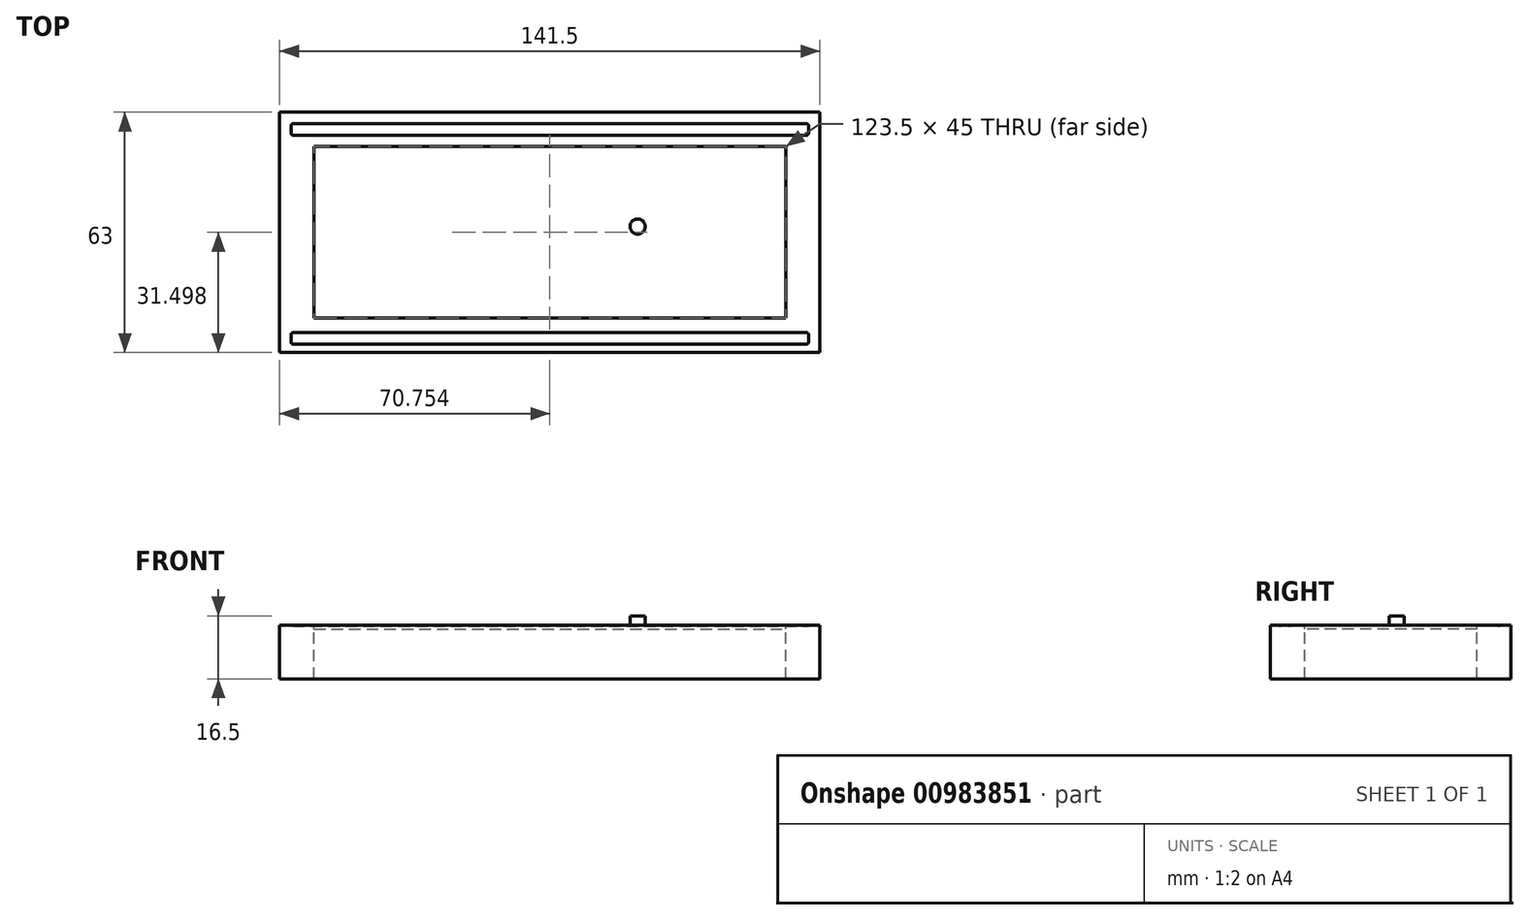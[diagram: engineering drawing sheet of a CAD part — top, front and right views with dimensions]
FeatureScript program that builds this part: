
annotation { "Feature Type Name" : "Feature", "Feature Type Description" : "" }
export const myFeature = defineFeature(function(context is Context, id is Id, definition is map)
    precondition{}
    {
        {
            var Q0;
            Q0=qCreatedBy(makeId("Top.planeOp"),FACE);
            var sketch = newSketch(context, id + "F0", { "sketchPlane" : qUnion([Q0])});
            skLineSegment(sketch, "E0.bottom", {"start": v(-3, 3) * mm, "end": v(3, 3) * mm});
            skLineSegment(sketch, "E0.top", {"start": v(-3, -3) * mm, "end": v(3, -3) * mm});
            skLineSegment(sketch, "E0.left", {"start": v(-3, 3) * mm, "end": v(-3, -3) * mm});
            skLineSegment(sketch, "E0.right", {"start": v(3, 3) * mm, "end": v(3, -3) * mm});
            skLineSegment(sketch, "E1", {"start": v(0, 3) * mm, "end": v(0, -3) * mm, "construction": true});
            skLineSegment(sketch, "E2", {"start": v(-3, 0) * mm, "end": v(3, 0) * mm, "construction": true});
            skSolve(sketch);
        }
        {
            var Q0;
            Q0=makeQuery(id+"F0.imprint","IMPRINT",FACE,{"disambiguationData":[TD([[makeQuery(id+"F0.imprint","IMPRINT",EDGE,{"derivedFrom":sQuery(id+"F0.wireOp",EDGE,"E0.bottom")}),-1.0]])]});
            extrude(context, id + "F1", {"entities" : qUnion([Q0]), "oppositeDirection" : true, "depth" : 3.5 * mm, "offsetDistance" : 25 * mm});
        }
        {
            var Q0;
            Q0=makeQuery(id+"F1.opExtrude","CAP_FACE",FACE,{"disambiguationData":[OSD([sQuery(id+"F0.wireOp",EDGE,"E0.bottom"),sQuery(id+"F0.wireOp",EDGE,"E0.top"),sQuery(id+"F0.wireOp",EDGE,"E0.left"),sQuery(id+"F0.wireOp",EDGE,"E0.right")])],"isStart":true});
            var sketch = newSketch(context, id + "F2", { "sketchPlane" : qUnion([Q0])});
            skCircle(sketch, "E3", {"center": v(0, 0) * mm, "radius": 2 * mm});
            skSolve(sketch);
        }
        {
            var Q0;
            Q0=makeQuery(id+"F2.imprint","IMPRINT",FACE,{"disambiguationData":[TD([[makeQuery(id+"F2.imprint","IMPRINT",EDGE,{"derivedFrom":sQuery(id+"F2.wireOp",EDGE,"E3")}),1.0]])]});
            extrude(context, id + "F3", {"entities" : qUnion([Q0]), "operationType" : NewBodyOperationType.ADD, "depth" : 2.5 * mm, "offsetDistance" : 25 * mm});
        }
        {
            var Q0;
            Q0=qCreatedBy(makeId("Top.planeOp"),FACE);
            var sketch = newSketch(context, id + "F4", { "sketchPlane" : qUnion([Q0])});
            skLineSegment(sketch, "E4.bottom", {"start": v(-84.76, 20.98) * mm, "end": v(38.74, 20.98) * mm});
            skLineSegment(sketch, "E4.top", {"start": v(-84.76, -24.02) * mm, "end": v(38.74, -24.02) * mm});
            skLineSegment(sketch, "E4.left", {"start": v(-84.76, 20.98) * mm, "end": v(-84.76, -24.02) * mm});
            skLineSegment(sketch, "E4.right", {"start": v(38.74, 20.98) * mm, "end": v(38.74, -24.02) * mm});
            skLineSegment(sketch, "E5", {"start": v(-23, 20.98) * mm, "end": v(-23, -24.02) * mm, "construction": true});
            skLineSegment(sketch, "E6", {"start": v(-84.76, -1.52) * mm, "end": v(38.74, -1.52) * mm, "construction": true});
            skSolve(sketch);
        }
        {
            var Q0;
            Q0=makeQuery(id+"F4.imprint","IMPRINT",FACE,{"disambiguationData":[TD([[makeQuery(id+"F4.imprint","IMPRINT",EDGE,{"derivedFrom":sQuery(id+"F4.wireOp",EDGE,"E4.bottom")}),-1.0]])]});
            extrude(context, id + "F5", {"entities" : qUnion([Q0]), "oppositeDirection" : true, "depth" : 14 * mm, "offsetDistance" : 25 * mm});
        }
        {
            var Q0;
            Q0=makeQuery(id+"F5.opExtrude","CAP_FACE",FACE,{"disambiguationData":[OSD([sQuery(id+"F4.wireOp",EDGE,"E4.bottom"),sQuery(id+"F4.wireOp",EDGE,"E4.top"),sQuery(id+"F4.wireOp",EDGE,"E4.left"),sQuery(id+"F4.wireOp",EDGE,"E4.right")])],"isStart":true});
            var sketch = newSketch(context, id + "F6", { "sketchPlane" : qUnion([Q0])});
            skLineSegment(sketch, "E7.0", {"start": v(-93.76, 29.98) * mm, "end": v(-93.76, -33.02) * mm});
            skLineSegment(sketch, "E7.1", {"start": v(47.74, 29.98) * mm, "end": v(-93.76, 29.98) * mm});
            skLineSegment(sketch, "E7.2", {"start": v(47.74, -33.02) * mm, "end": v(47.74, 29.98) * mm});
            skLineSegment(sketch, "E7.3", {"start": v(-93.76, -33.02) * mm, "end": v(47.74, -33.02) * mm});
            skSolve(sketch);
        }
        {
            var Q0;
            Q0=makeQuery(id+"F6.imprint","IMPRINT",FACE,{"disambiguationData":[TD([[makeQuery(id+"F6.imprint","IMPRINT",EDGE,{"derivedFrom":sQuery(id+"F6.wireOp",EDGE,"E7.0")}),1.0]])]});
            extrude(context, id + "F7", {"entities" : qUnion([Q0]), "operationType" : NewBodyOperationType.ADD, "oppositeDirection" : true, "depth" : 14 * mm, "offsetDistance" : 25 * mm});
        }
        {
            var Q0;
            Q0 = qSketchRegion(id + "F2", true);
            var Q1;
            Q1 = qSketchRegion(id + "F4", true);
            extrude(context, id + "F8", {"entities" : qUnion([Q0, Q1]), "operationType" : NewBodyOperationType.REMOVE, "oppositeDirection" : true, "depth" : 14 * mm, "offsetDistance" : 25 * mm});
        }
        {
            var Q0;
            Q0 = qSketchRegion(id + "F4", true);
            extrude(context, id + "F9", {"entities" : qUnion([Q0]), "oppositeDirection" : true, "depth" : 1 * mm, "offsetDistance" : 25 * mm});
        }
        {
            var Q0;
            Q0=makeQuery(id+"F6.imprint","IMPRINT",FACE,{"disambiguationData":[TD([[makeQuery(id+"F6.imprint","IMPRINT",EDGE,{"derivedFrom":sQuery(id+"F6.wireOp",EDGE,"E7.0")}),1.0]])]});
            var sketch = newSketch(context, id + "F10", { "sketchPlane" : qUnion([Q0])});
            skLineSegment(sketch, "E8.bottom", {"start": v(-90.76, 26.94) * mm, "end": v(44.74, 26.94) * mm});
            skLineSegment(sketch, "E8.top", {"start": v(-90.76, 23.94) * mm, "end": v(44.74, 23.94) * mm});
            skLineSegment(sketch, "E8.left", {"start": v(-90.76, 26.94) * mm, "end": v(-90.76, 23.94) * mm});
            skLineSegment(sketch, "E8.right", {"start": v(44.74, 26.94) * mm, "end": v(44.74, 23.94) * mm});
            skLineSegment(sketch, "E9.bottom", {"start": v(-90.76, -27.8) * mm, "end": v(44.74, -27.8) * mm});
            skLineSegment(sketch, "E9.top", {"start": v(-90.76, -30.8) * mm, "end": v(44.74, -30.8) * mm});
            skLineSegment(sketch, "E9.left", {"start": v(-90.76, -27.8) * mm, "end": v(-90.76, -30.8) * mm});
            skLineSegment(sketch, "E9.right", {"start": v(44.74, -27.8) * mm, "end": v(44.74, -30.8) * mm});
            skSolve(sketch);
        }
        {
            var Q0;
            Q0 = qSketchRegion(id + "F10", true);
            extrude(context, id + "F11", {"entities" : qUnion([Q0]), "operationType" : NewBodyOperationType.REMOVE, "oppositeDirection" : true, "depth" : .2 * mm, "offsetDistance" : 25 * mm});
        }
        {
            var Q0;
            Q0=makeQuery(id+"F11.boolean.opBoolean","COPY",EDGE,{"derivedFrom":makeQuery(id+"F11.opExtrude","SWEPT_EDGE",EDGE,{"disambiguationData":[OSD([sQuery(id+"F10.wireOp",EDGE,"E8.bottom"),sQuery(id+"F10.wireOp",EDGE,"E8.left")])]})});
            var Q1;
            Q1=makeQuery(id+"F11.boolean.opBoolean","COPY",EDGE,{"derivedFrom":makeQuery(id+"F11.opExtrude","SWEPT_EDGE",EDGE,{"disambiguationData":[OSD([sQuery(id+"F10.wireOp",EDGE,"E8.top"),sQuery(id+"F10.wireOp",EDGE,"E8.left")])]})});
            var Q2;
            Q2=makeQuery(id+"F11.boolean.opBoolean","COPY",EDGE,{"derivedFrom":makeQuery(id+"F11.opExtrude","SWEPT_EDGE",EDGE,{"disambiguationData":[OSD([sQuery(id+"F10.wireOp",EDGE,"E8.top"),sQuery(id+"F10.wireOp",EDGE,"E8.right")])]})});
            var Q3;
            Q3=makeQuery(id+"F11.boolean.opBoolean","COPY",EDGE,{"derivedFrom":makeQuery(id+"F11.opExtrude","SWEPT_EDGE",EDGE,{"disambiguationData":[OSD([sQuery(id+"F10.wireOp",EDGE,"E8.bottom"),sQuery(id+"F10.wireOp",EDGE,"E8.right")])]})});
            var Q4;
            Q4=makeQuery(id+"F11.boolean.opBoolean","COPY",EDGE,{"derivedFrom":makeQuery(id+"F11.opExtrude","SWEPT_EDGE",EDGE,{"disambiguationData":[OSD([sQuery(id+"F10.wireOp",EDGE,"E9.bottom"),sQuery(id+"F10.wireOp",EDGE,"E9.left")])]})});
            var Q5;
            Q5=makeQuery(id+"F11.boolean.opBoolean","COPY",EDGE,{"derivedFrom":makeQuery(id+"F11.opExtrude","SWEPT_EDGE",EDGE,{"disambiguationData":[OSD([sQuery(id+"F10.wireOp",EDGE,"E9.top"),sQuery(id+"F10.wireOp",EDGE,"E9.left")])]})});
            var Q6;
            Q6=makeQuery(id+"F11.boolean.opBoolean","COPY",EDGE,{"derivedFrom":makeQuery(id+"F11.opExtrude","SWEPT_EDGE",EDGE,{"disambiguationData":[OSD([sQuery(id+"F10.wireOp",EDGE,"E9.bottom"),sQuery(id+"F10.wireOp",EDGE,"E9.right")])]})});
            var Q7;
            Q7=makeQuery(id+"F11.boolean.opBoolean","COPY",EDGE,{"derivedFrom":makeQuery(id+"F11.opExtrude","SWEPT_EDGE",EDGE,{"disambiguationData":[OSD([sQuery(id+"F10.wireOp",EDGE,"E9.top"),sQuery(id+"F10.wireOp",EDGE,"E9.right")])]})});
            fillet(context, id + "F12", {"entities" : qUnion([Q0, Q1, Q2, Q3, Q4, Q5, Q6, Q7]), "radius" : .5 * mm, "tangentPropagation" : true, "allowEdgeOverflow" : false});
        }
    });
